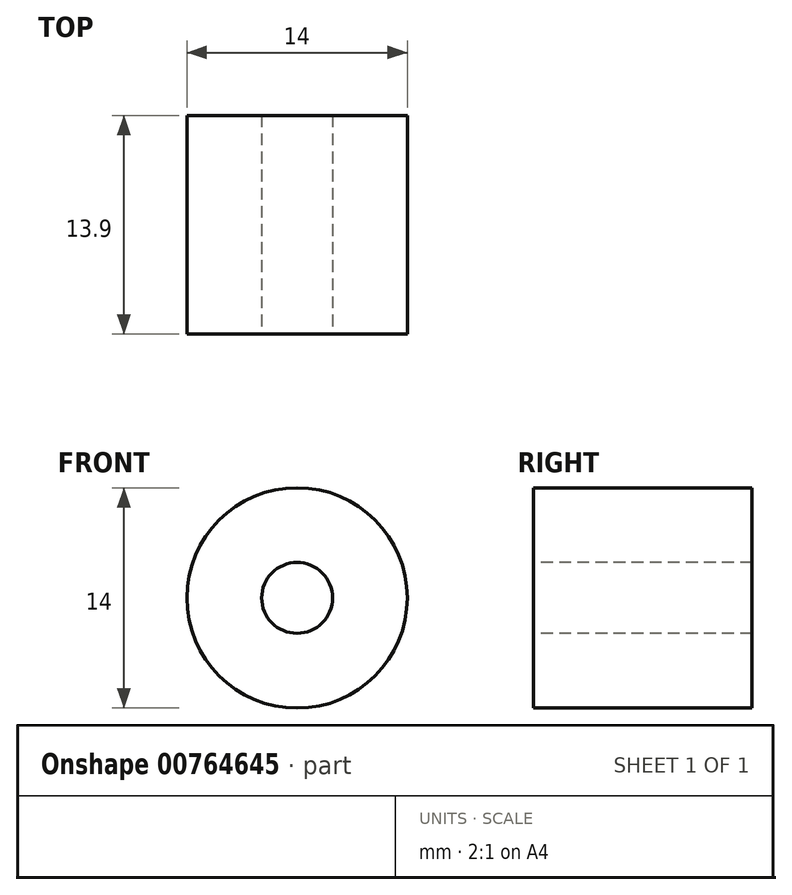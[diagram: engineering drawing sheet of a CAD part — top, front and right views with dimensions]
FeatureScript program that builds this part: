
annotation { "Feature Type Name" : "Feature", "Feature Type Description" : "" }
export const myFeature = defineFeature(function(context is Context, id is Id, definition is map)
    precondition{}
    {
        {
            var Q0;
            Q0=qCreatedBy(makeId("Front.planeOp"),FACE);
            var sketch = newSketch(context, id + "F0", { "sketchPlane" : qUnion([Q0])});
            skCircle(sketch, "E0", {"center": v(0, 0) * mm, "radius": 9 * mm});
            skCircle(sketch, "E1", {"center": v(0, 0) * mm, "radius": 7 * mm});
            skCircle(sketch, "E2", {"center": v(0, 0) * mm, "radius": 2.25 * mm});
            skSolve(sketch);
        }
        {
            var Q0;
            Q0=sQuery(id+"F0.wireOp",EDGE,"E1");
            var Q1;
            Q1=sQuery(id+"F0.wireOp",EDGE,"E2");
            extrude(context, id + "F1", {"bodyType" : ToolBodyType.SURFACE, "surfaceEntities" : qUnion([Q0, Q1]), "depth" : 13.9 * mm, "offsetDistance" : 25 * mm});
        }
    });
